# Revit family: Door-Exterior-Simpson-Nantucket-Quarter_Arch_Glass-Single
name_source: partatom
category: Doors
revit_build: Autodesk Revit Architecture 2012 (Build: 20110916_2132(x64)
units: mm (PartAtom-declared; Revit-internal decimal feet)

## types (42) — shared parameters
Assembly Code = B2030230
Bottom Rail Height = 0' - 8 11/16"
Bottom of Arch = 0' - 9 19/32"
Construction Type = Wood
Description = Nantucket Exterior Door
Frame = Wood - Simpson Doors - Douglas Fir
Frame Projection Ext. = 0' - 1"
Frame Projection Int. = 0' - 1"
Frame Type = Frame : Standard
Frame Width = 0' - 3"
Function = Exterior
Glass = Glass - Simpson Doors - Clear
Glass Options = http://simpsondoor.com
Innerbond Double Hip-Raised Panel = No
Lower Panel = Wood - Simpson Doors - Douglas Fir
Manufacturer = Simpsons Door Company
Middle Rail Height = 0' - 4 1/2"
Muntin Width = 0' - 0 7/8"
Number of Horizontal Muntins = 1
Number of Panel Dividers = 1
Ovolo Construction = Yes
Panel = Wood - Simpson Doors - Douglas Fir
Panel Divider Width = 0' - 3 1/2"
Panel Stile Width = 0' - 5"
Product Documentation Link = http://www.simpsondoor.com
Product Page URL = http://www.simpsondoor.com
Thickness = 0' - 1 3/4"
Thickness Note = comes in 1 3/4" and 2 1/4" Thickness. Default is set to 1 3/4"
Top Rail Height = 0' - 4 15/16"
URL = http://www.simpsondoor.com
Wall Closure = By host
Window Bottom Offset = 6' - 1 3/16"
Window Height = 1' - 6 1/2"
Wood Species = http://simpsondoor.com

## per-type parameters (varying)
| type | Height | Model | Number of Vertical Muntins | Rough Height | Rough Width | Width |
| 77660 Nantucket 30x80 Ovolo Flat Panel | 6' - 8" | 77660 | 2 | 6' - 10" | 2' - 10" | 2' - 6" |
| 77660 Nantucket 30x84 Ovolo Flat Panel | 7' - 0" | 77660 | 2 | 7' - 2" | 2' - 10" | 2' - 6" |
| 77660 Nantucket 30x96 Ovolo Flat Panel | 8' - 0" | 77660 | 2 | 8' - 2" | 2' - 10" | 2' - 6" |
| 77660 Nantucket 32x80 Ovolo Flat Panel | 6' - 8" | 77660 | 2 | 6' - 10" | 3' - 0" | 2' - 8" |
| 77660 Nantucket 32x84 Ovolo Flat Panel | 7' - 0" | 77660 | 2 | 7' - 2" | 3' - 0" | 2' - 8" |
| 77660 Nantucket 32x96 Ovolo Flat Panel | 8' - 0" | 77660 | 2 | 8' - 2" | 3' - 0" | 2' - 8" |
| 77660 Nantucket 34x80 Ovolo Flat Panel | 6' - 8" | 77660 | 2 | 6' - 10" | 3' - 2" | 2' - 10" |
| 77660 Nantucket 34x84 Ovolo Flat Panel | 7' - 0" | 77660 | 2 | 7' - 2" | 3' - 2" | 2' - 10" |
| 77660 Nantucket 34x96 Ovolo Flat Panel | 8' - 0" | 77660 | 2 | 8' - 2" | 3' - 2" | 2' - 10" |
| 77660 Nantucket 36x80 Ovolo Flat Panel | 6' - 8" | 77660 | 2 | 6' - 10" | 3' - 4" | 3' - 0" |
| 77660 Nantucket 36x84 Ovolo Flat Panel | 7' - 0" | 77660 | 2 | 7' - 2" | 3' - 4" | 3' - 0" |
| 77660 Nantucket 36x96 Ovolo Flat Panel | 8' - 0" | 77660 | 2 | 8' - 2" | 3' - 4" | 3' - 0" |
| 77660 Nantucket 38x80 Ovolo Flat Panel | 6' - 8" | 77660 | 2 | 6' - 10" | 3' - 6" | 3' - 2" |
| 77660 Nantucket 38x84 Ovolo Flat Panel | 7' - 0" | 77660 | 2 | 7' - 2" | 3' - 6" | 3' - 2" |
| 77660 Nantucket 38x96 Ovolo Flat Panel | 8' - 0" | 77660 | 2 | 8' - 2" | 3' - 6" | 3' - 2" |
| 77660 Nantucket 40x80 Ovolo Flat Panel | 6' - 8" | 77660 | 2 | 6' - 10" | 3' - 8" | 3' - 4" |
| 77660 Nantucket 40x84 Ovolo Flat Panel | 7' - 0" | 77660 | 2 | 7' - 2" | 3' - 8" | 3' - 4" |
| 77660 Nantucket 40x96 Ovolo Flat Panel | 8' - 0" | 77660 | 2 | 8' - 2" | 3' - 8" | 3' - 4" |
| 77660 Nantucket 42x80 Ovolo Flat Panel | 6' - 8" | 77660 | 2 | 6' - 10" | 3' - 10" | 3' - 6" |
| 77660 Nantucket 42x84 Ovolo Flat Panel | 7' - 0" | 77660 | 2 | 7' - 2" | 3' - 10" | 3' - 6" |
| 77660 Nantucket 42x96 Ovolo Flat Panel | 8' - 0" | 77660 | 2 | 8' - 2" | 3' - 10" | 3' - 6" |
| 77684 Nantucket 30x80 Ovolo Flat Panel | 6' - 8" | 77684 | 1 | 6' - 10" | 2' - 10" | 2' - 6" |
| 77684 Nantucket 30x84 Ovolo Flat Panel | 7' - 0" | 77684 | 1 | 7' - 2" | 2' - 10" | 2' - 6" |
| 77684 Nantucket 30x96 Ovolo Flat Panel | 8' - 0" | 77684 | 1 | 8' - 2" | 2' - 10" | 2' - 6" |
| 77684 Nantucket 32x80 Ovolo Flat Panel | 6' - 8" | 77684 | 1 | 6' - 10" | 3' - 0" | 2' - 8" |
| 77684 Nantucket 32x84 Ovolo Flat Panel | 7' - 0" | 77684 | 1 | 7' - 2" | 3' - 0" | 2' - 8" |
| 77684 Nantucket 32x96 Ovolo Flat Panel | 8' - 0" | 77684 | 1 | 8' - 2" | 3' - 0" | 2' - 8" |
| 77684 Nantucket 34x80 Ovolo Flat Panel | 6' - 8" | 77684 | 1 | 6' - 10" | 3' - 2" | 2' - 10" |
| 77684 Nantucket 34x84 Ovolo Flat Panel | 7' - 0" | 77684 | 1 | 7' - 2" | 3' - 2" | 2' - 10" |
| 77684 Nantucket 34x96 Ovolo Flat Panel | 8' - 0" | 77684 | 1 | 8' - 2" | 3' - 2" | 2' - 10" |
| 77684 Nantucket 36x80 Ovolo Flat Panel | 6' - 8" | 77684 | 1 | 6' - 10" | 3' - 4" | 3' - 0" |
| 77684 Nantucket 36x84 Ovolo Flat Panel | 7' - 0" | 77684 | 1 | 7' - 2" | 3' - 4" | 3' - 0" |
| 77684 Nantucket 36x96 Ovolo Flat Panel | 8' - 0" | 77684 | 1 | 8' - 2" | 3' - 4" | 3' - 0" |
| 77684 Nantucket 38x80 Ovolo Flat Panel | 6' - 8" | 77684 | 1 | 6' - 10" | 3' - 6" | 3' - 2" |
| 77684 Nantucket 38x84 Ovolo Flat Panel | 7' - 0" | 77684 | 1 | 7' - 2" | 3' - 6" | 3' - 2" |
| 77684 Nantucket 38x96 Ovolo Flat Panel | 8' - 0" | 77684 | 1 | 8' - 2" | 3' - 6" | 3' - 2" |
| 77684 Nantucket 40x80 Ovolo Flat Panel | 6' - 8" | 77684 | 1 | 6' - 10" | 3' - 8" | 3' - 4" |
| 77684 Nantucket 40x84 Ovolo Flat Panel | 7' - 0" | 77684 | 1 | 7' - 2" | 3' - 8" | 3' - 4" |
| 77684 Nantucket 40x96 Ovolo Flat Panel | 8' - 0" | 77684 | 1 | 8' - 2" | 3' - 8" | 3' - 4" |
| 77684 Nantucket 42x80 Ovolo Flat Panel | 6' - 8" | 77684 | 1 | 6' - 10" | 3' - 10" | 3' - 6" |
| 77684 Nantucket 42x84 Ovolo Flat Panel | 7' - 0" | 77684 | 1 | 7' - 2" | 3' - 10" | 3' - 6" |
| 77684 Nantucket 42x96 Ovolo Flat Panel | 8' - 0" | 77684 | 1 | 8' - 2" | 3' - 10" | 3' - 6" |

## geometry (parser evidence)
native form markers: Blend x8, Sweep x19
no freeform markers — native parametric forms only
